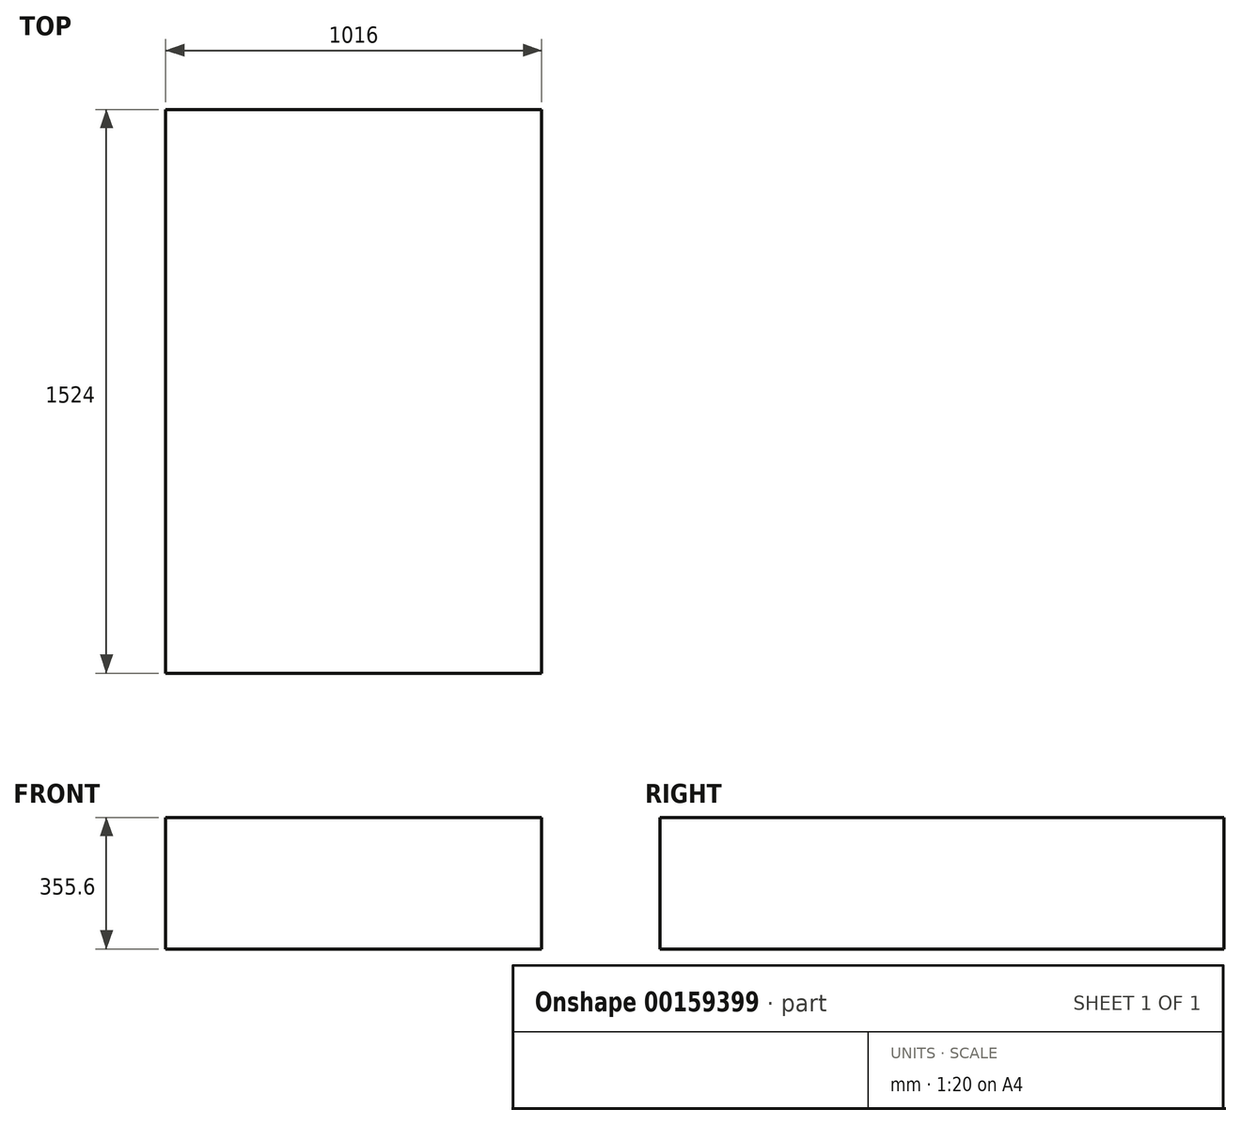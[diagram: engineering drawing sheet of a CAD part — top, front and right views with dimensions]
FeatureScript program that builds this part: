
annotation { "Feature Type Name" : "Feature", "Feature Type Description" : "" }
export const myFeature = defineFeature(function(context is Context, id is Id, definition is map)
    precondition{}
    {
        {
            var Q0;
            Q0=qCreatedBy(makeId("Top.planeOp"),FACE);
            var sketch = newSketch(context, id + "F0", { "sketchPlane" : qUnion([Q0])});
            skLineSegment(sketch, "E0.bottom", {"start": v(601.88, 793.57) * mm, "end": v(-414.12, 793.57) * mm});
            skLineSegment(sketch, "E0.top", {"start": v(601.88, -730.43) * mm, "end": v(-414.12, -730.43) * mm});
            skLineSegment(sketch, "E0.left", {"start": v(601.88, 793.57) * mm, "end": v(601.88, -730.43) * mm});
            skLineSegment(sketch, "E0.right", {"start": v(-414.12, 793.57) * mm, "end": v(-414.12, -730.43) * mm});
            skSolve(sketch);
        }
        {
            var Q0;
            Q0 = qSketchRegion(id + "F0", true);
            extrude(context, id + "F1", {"entities" : qUnion([Q0]), "depth" : 355.6 * mm});
        }
    });
